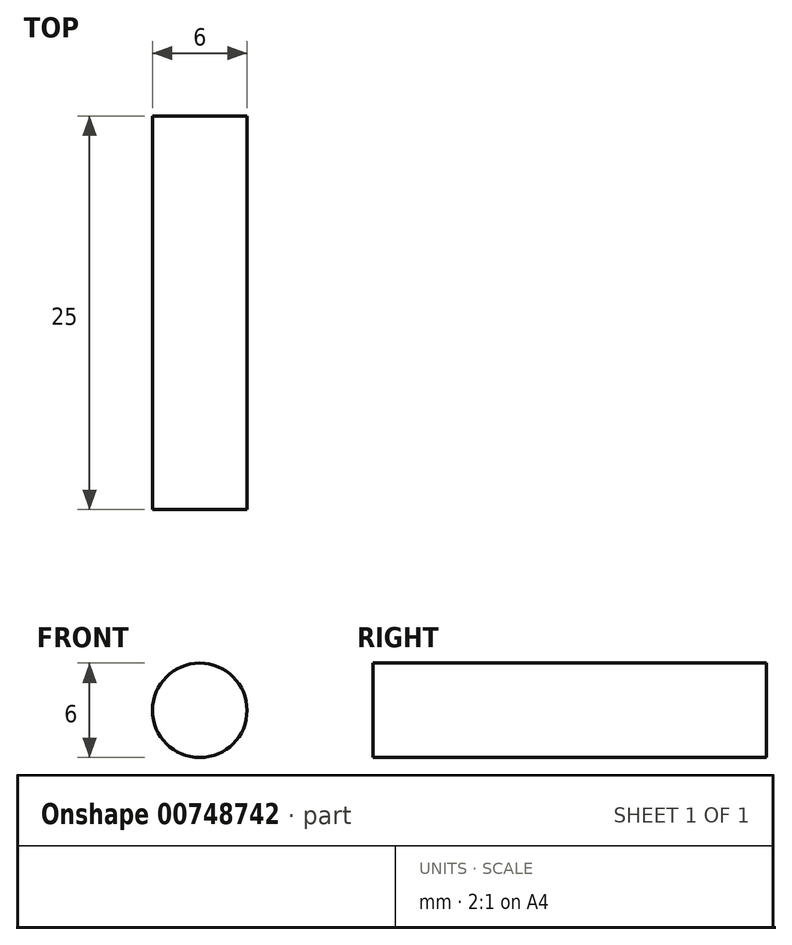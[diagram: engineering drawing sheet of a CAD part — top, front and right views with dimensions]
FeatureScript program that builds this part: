
annotation { "Feature Type Name" : "Feature", "Feature Type Description" : "" }
export const myFeature = defineFeature(function(context is Context, id is Id, definition is map)
    precondition{}
    {
        {
            var Q0;
            Q0=qCreatedBy(makeId("Front.planeOp"),FACE);
            var sketch = newSketch(context, id + "F0", { "sketchPlane" : qUnion([Q0])});
            skCircle(sketch, "E0", {"center": v(0, 0) * mm, "radius": 3 * mm});
            skSolve(sketch);
        }
        {
            var Q0;
            Q0=qSketchRegion(id+"F0",true);
            extrude(context, id + "F1", {"entities" : qUnion([Q0]), "depth" : 25 * mm});
        }
    });
